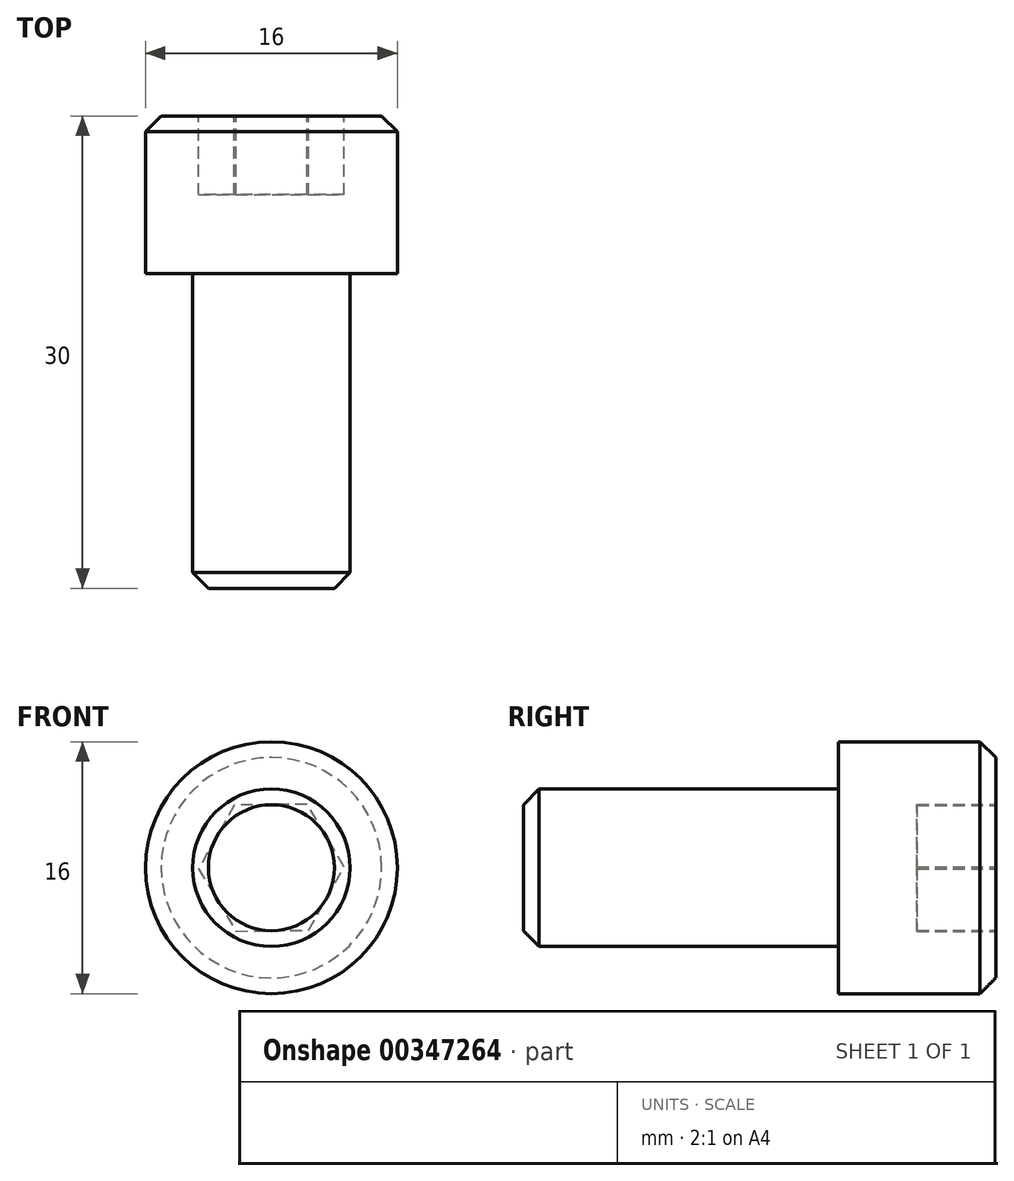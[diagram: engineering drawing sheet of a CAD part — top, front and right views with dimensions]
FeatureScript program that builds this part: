
annotation { "Feature Type Name" : "Feature", "Feature Type Description" : "" }
export const myFeature = defineFeature(function(context is Context, id is Id, definition is map)
    precondition{}
    {
        {
            var Q0;
            Q0=qCreatedBy(makeId("Front.planeOp"),FACE);
            var sketch = newSketch(context, id + "F0", { "sketchPlane" : qUnion([Q0])});
            skCircle(sketch, "E0", {"center": v(0, 0) * mm, "radius": 8 * mm});
            skSolve(sketch);
        }
        {
            var Q0;
            Q0=makeQuery(id+"F0.imprint","IMPRINT",FACE,{"disambiguationData":[TD([[makeQuery(id+"F0.imprint","IMPRINT",EDGE,{"derivedFrom":sQuery(id+"F0.wireOp",EDGE,"E0")}),1.0]])]});
            extrude(context, id + "F1", {"entities" : qUnion([Q0]), "depth" : 10 * mm});
        }
        {
            var Q0;
            Q0=makeQuery(id+"F1.opExtrude","CAP_FACE",FACE,{"disambiguationData":[OSD([sQuery(id+"F0.wireOp",EDGE,"E0")])],"isStart":false});
            var sketch = newSketch(context, id + "F2", { "sketchPlane" : qUnion([Q0])});
            skCircle(sketch, "E1", {"center": v(0, 0) * mm, "radius": 5 * mm});
            skSolve(sketch);
        }
        {
            var Q0;
            Q0=makeQuery(id+"F2.imprint","IMPRINT",FACE,{"disambiguationData":[TD([[makeQuery(id+"F2.imprint","IMPRINT",EDGE,{"derivedFrom":sQuery(id+"F2.wireOp",EDGE,"E1")}),1.0]])]});
            extrude(context, id + "F3", {"entities" : qUnion([Q0]), "operationType" : NewBodyOperationType.ADD, "depth" : 20 * mm});
        }
        {
            var Q0;
            Q0=makeQuery(id+"F3.opExtrude","CAP_EDGE",EDGE,{"disambiguationData":[OSD([sQuery(id+"F2.wireOp",EDGE,"E1")])],"isStart":false});
            var Q1;
            Q1=makeQuery(id+"F1.opExtrude","CAP_EDGE",EDGE,{"disambiguationData":[OSD([sQuery(id+"F0.wireOp",EDGE,"E0")])],"isStart":true});
            chamfer(context, id + "F4", {"entities" : qUnion([Q0, Q1]), "width" : 1 * mm, "tangentPropagation" : true});
        }
        {
            var Q0;
            Q0=makeQuery(id+"F1.opExtrude","CAP_FACE",FACE,{"disambiguationData":[OSD([sQuery(id+"F0.wireOp",EDGE,"E0")])],"isStart":true});
            var sketch = newSketch(context, id + "F5", { "sketchPlane" : qUnion([Q0])});
            skCircle(sketch, "E2", {"center": v(0, 0) * mm, "radius": 4 * mm, "construction": true});
            skLineSegment(sketch, "E3.0", {"start": v(-2.36, -3.97) * mm, "end": v(-4.62, 0.06) * mm});
            skLineSegment(sketch, "E3.1", {"start": v(-4.62, 0.06) * mm, "end": v(-2.26, 4.03) * mm});
            skLineSegment(sketch, "E3.2", {"start": v(-2.26, 4.03) * mm, "end": v(2.36, 3.97) * mm});
            skLineSegment(sketch, "E3.3", {"start": v(2.36, 3.97) * mm, "end": v(4.62, -0.06) * mm});
            skLineSegment(sketch, "E3.4", {"start": v(4.62, -0.06) * mm, "end": v(2.26, -4.03) * mm});
            skLineSegment(sketch, "E3.5", {"start": v(2.26, -4.03) * mm, "end": v(-2.36, -3.97) * mm});
            skPoint(sketch, "E3.0.midPoint", {"position": v(-3.5, -1.95) * mm});
            skSolve(sketch);
        }
        {
            var Q0;
            Q0=makeQuery(id+"F5.imprint","IMPRINT",FACE,{"disambiguationData":[TD([[makeQuery(id+"F5.imprint","IMPRINT",EDGE,{"derivedFrom":sQuery(id+"F5.wireOp",EDGE,"E3.0")}),-1.0]])]});
            extrude(context, id + "F6", {"entities" : qUnion([Q0]), "operationType" : NewBodyOperationType.REMOVE, "oppositeDirection" : true, "depth" : 5 * mm});
        }
    });
